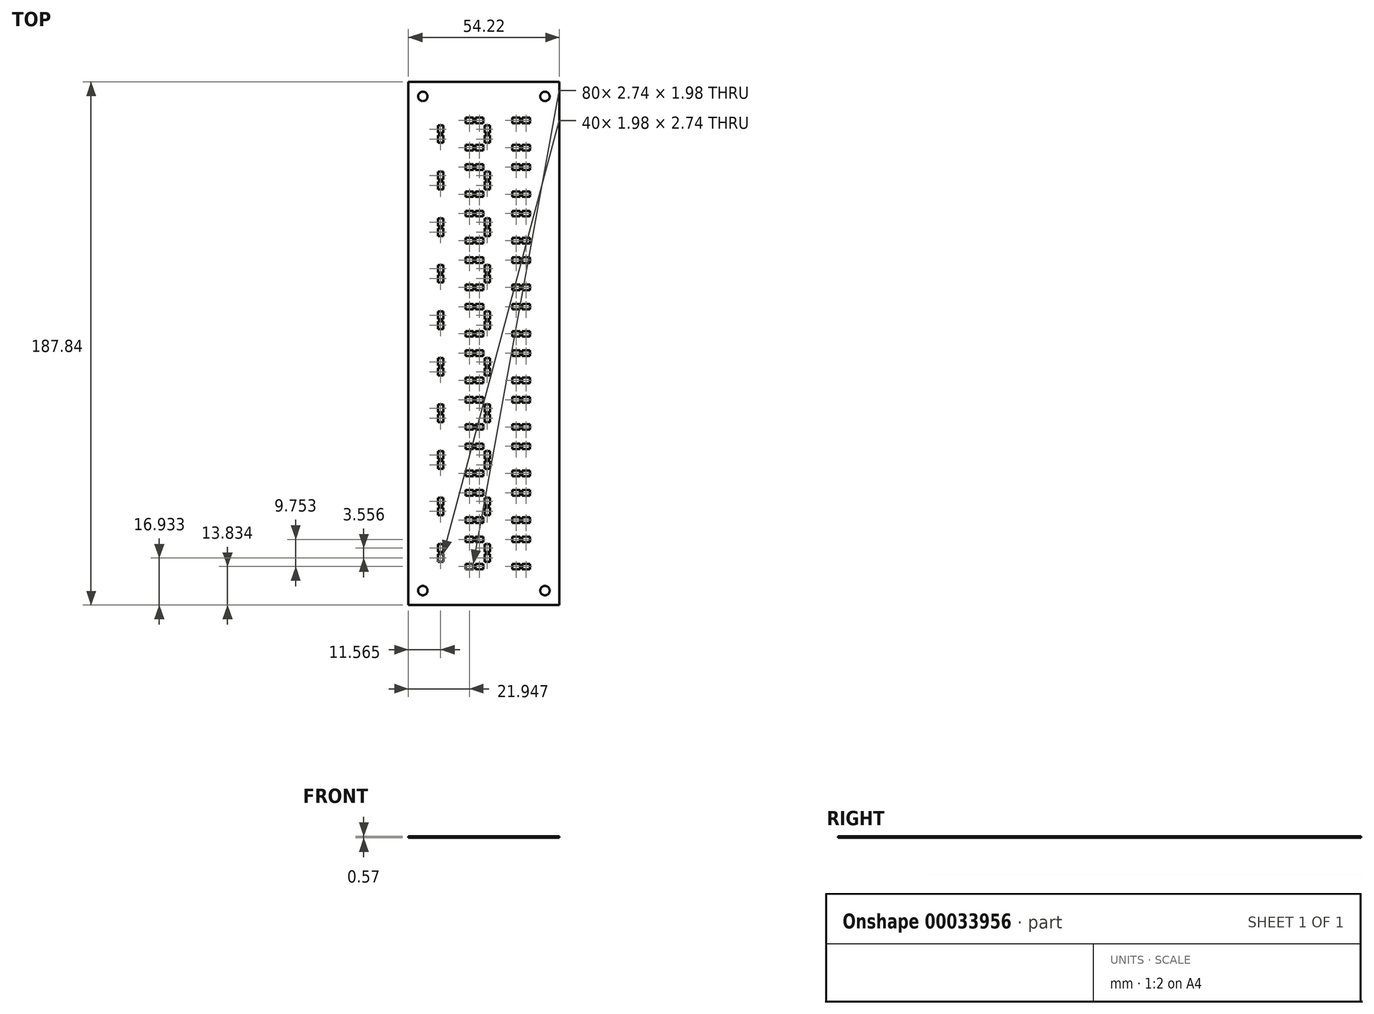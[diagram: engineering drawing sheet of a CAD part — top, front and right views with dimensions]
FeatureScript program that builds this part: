
annotation { "Feature Type Name" : "Feature", "Feature Type Description" : "" }
export const myFeature = defineFeature(function(context is Context, id is Id, definition is map)
    precondition{}
    {
        {
            var Q0;
            Q0=qCreatedBy(makeId("Top.planeOp"),FACE);
            var sketch = newSketch(context, id + "F0", { "sketchPlane" : qUnion([Q0])});
            skLineSegment(sketch, "E0.rect.bottom", {"start": v(-27.11, 93.92) * mm, "end": v(27.11, 93.92) * mm});
            skLineSegment(sketch, "E0.rect.top", {"start": v(-27.11, -93.92) * mm, "end": v(27.11, -93.92) * mm});
            skLineSegment(sketch, "E0.rect.left", {"start": v(-27.11, 93.92) * mm, "end": v(-27.11, -93.92) * mm});
            skLineSegment(sketch, "E0.rect.right", {"start": v(27.11, 93.92) * mm, "end": v(27.11, -93.92) * mm});
            skPoint(sketch, "E0.rect.middle", {"position": v(0, 0) * mm});
            skCircle(sketch, "E1", {"center": v(-21.92, 88.72) * mm, "radius": 1.69 * mm});
            skCircle(sketch, "E2", {"center": v(21.92, 88.72) * mm, "radius": 1.69 * mm});
            skCircle(sketch, "E3", {"center": v(21.92, -88.72) * mm, "radius": 1.69 * mm});
            skCircle(sketch, "E4", {"center": v(-21.92, -88.72) * mm, "radius": 1.69 * mm});
            skSolve(sketch);
        }
        {
            var Q0;
            Q0=qSketchRegion(id+"F0",true);
            extrude(context, id + "F1", {"entities" : qUnion([Q0]), "depth" : .57 * mm});
        }
        {
            var Q0;
            Q0=makeQuery(id+"F1.opExtrude","CAP_FACE",FACE,{"disambiguationData":[OSD([sQuery(id+"F0.wireOp",EDGE,"E0.rect.bottom"),sQuery(id+"F0.wireOp",EDGE,"E0.rect.top"),sQuery(id+"F0.wireOp",EDGE,"E0.rect.left"),sQuery(id+"F0.wireOp",EDGE,"E0.rect.right"),sQuery(id+"F0.wireOp",EDGE,"E1"),sQuery(id+"F0.wireOp",EDGE,"E2"),sQuery(id+"F0.wireOp",EDGE,"E3"),sQuery(id+"F0.wireOp",EDGE,"E4")])],"isStart":false});
            var sketch = newSketch(context, id + "F2", { "sketchPlane" : qUnion([Q0])});
            skLineSegment(sketch, "E5.bottom", {"start": v(-16.54, -78.36) * mm, "end": v(-14.55, -78.36) * mm});
            skLineSegment(sketch, "E5.top", {"start": v(-16.54, -75.62) * mm, "end": v(-14.55, -75.62) * mm});
            skLineSegment(sketch, "E5.left", {"start": v(-16.54, -78.36) * mm, "end": v(-16.54, -75.62) * mm});
            skLineSegment(sketch, "E5.right", {"start": v(-14.55, -78.36) * mm, "end": v(-14.55, -75.62) * mm});
            skLineSegment(sketch, "E6.bottom", {"start": v(-6.53, -79.1) * mm, "end": v(-3.8, -79.1) * mm});
            skLineSegment(sketch, "E6.top", {"start": v(-6.53, -81.08) * mm, "end": v(-3.8, -81.08) * mm});
            skLineSegment(sketch, "E6.left", {"start": v(-6.53, -79.1) * mm, "end": v(-6.53, -81.08) * mm});
            skLineSegment(sketch, "E6.right", {"start": v(-3.8, -79.1) * mm, "end": v(-3.8, -81.08) * mm});
            skLineSegment(sketch, "E7.bottom", {"start": v(-16.54, -74.8) * mm, "end": v(-14.55, -74.8) * mm});
            skLineSegment(sketch, "E7.top", {"start": v(-16.54, -72.06) * mm, "end": v(-14.55, -72.06) * mm});
            skLineSegment(sketch, "E7.left", {"start": v(-16.54, -74.8) * mm, "end": v(-16.54, -72.06) * mm});
            skLineSegment(sketch, "E7.right", {"start": v(-14.55, -74.8) * mm, "end": v(-14.55, -72.06) * mm});
            skLineSegment(sketch, "E8.left", {"start": v(-2.98, -79.1) * mm, "end": v(-2.98, -81.08) * mm});
            skLineSegment(sketch, "E8.top", {"start": v(-2.98, -81.08) * mm, "end": v(-0.24, -81.08) * mm});
            skLineSegment(sketch, "E8.right", {"start": v(-0.24, -79.1) * mm, "end": v(-0.24, -81.08) * mm});
            skLineSegment(sketch, "E8.bottom", {"start": v(-2.98, -79.1) * mm, "end": v(-0.24, -79.1) * mm});
            skLineSegment(sketch, "E9.top", {"start": v(-2.98, -71.32) * mm, "end": v(-0.24, -71.32) * mm});
            skLineSegment(sketch, "E10.right", {"start": v(-3.8, -69.34) * mm, "end": v(-3.8, -71.32) * mm});
            skLineSegment(sketch, "E9.left", {"start": v(-2.98, -69.34) * mm, "end": v(-2.98, -71.32) * mm});
            skLineSegment(sketch, "E10.top", {"start": v(-6.53, -71.32) * mm, "end": v(-3.8, -71.32) * mm});
            skLineSegment(sketch, "E10.bottom", {"start": v(-6.53, -69.34) * mm, "end": v(-3.8, -69.34) * mm});
            skLineSegment(sketch, "E9.bottom", {"start": v(-2.98, -69.34) * mm, "end": v(-0.24, -69.34) * mm});
            skLineSegment(sketch, "E9.right", {"start": v(-0.24, -69.34) * mm, "end": v(-0.24, -71.32) * mm});
            skLineSegment(sketch, "E10.left", {"start": v(-6.53, -69.34) * mm, "end": v(-6.53, -71.32) * mm});
            skLineSegment(sketch, "E11.top", {"start": v(13.79, -71.32) * mm, "end": v(16.53, -71.32) * mm});
            skLineSegment(sketch, "E12.top", {"start": v(13.79, -81.08) * mm, "end": v(16.53, -81.08) * mm});
            skLineSegment(sketch, "E11.right", {"start": v(16.53, -69.34) * mm, "end": v(16.53, -71.32) * mm});
            skLineSegment(sketch, "E11.bottom", {"start": v(13.79, -69.34) * mm, "end": v(16.53, -69.34) * mm});
            skLineSegment(sketch, "E13.right", {"start": v(2.21, -78.36) * mm, "end": v(2.21, -75.62) * mm});
            skLineSegment(sketch, "E13.left", {"start": v(0.23, -78.36) * mm, "end": v(0.23, -75.62) * mm});
            skLineSegment(sketch, "E13.top", {"start": v(0.23, -75.62) * mm, "end": v(2.21, -75.62) * mm});
            skLineSegment(sketch, "E13.bottom", {"start": v(0.23, -78.36) * mm, "end": v(2.21, -78.36) * mm});
            skLineSegment(sketch, "E12.bottom", {"start": v(13.79, -79.1) * mm, "end": v(16.53, -79.1) * mm});
            skLineSegment(sketch, "E12.right", {"start": v(16.53, -79.1) * mm, "end": v(16.53, -81.08) * mm});
            skLineSegment(sketch, "E14.top", {"start": v(0.23, -72.06) * mm, "end": v(2.21, -72.06) * mm});
            skLineSegment(sketch, "E14.bottom", {"start": v(0.23, -74.8) * mm, "end": v(2.21, -74.8) * mm});
            skLineSegment(sketch, "E11.left", {"start": v(13.79, -69.34) * mm, "end": v(13.79, -71.32) * mm});
            skLineSegment(sketch, "E15.bottom", {"start": v(10.23, -69.34) * mm, "end": v(12.98, -69.34) * mm});
            skLineSegment(sketch, "E15.right", {"start": v(12.98, -69.34) * mm, "end": v(12.98, -71.32) * mm});
            skLineSegment(sketch, "E15.top", {"start": v(10.23, -71.32) * mm, "end": v(12.98, -71.32) * mm});
            skLineSegment(sketch, "E15.left", {"start": v(10.23, -69.34) * mm, "end": v(10.23, -71.32) * mm});
            skLineSegment(sketch, "E12.left", {"start": v(13.79, -79.1) * mm, "end": v(13.79, -81.08) * mm});
            skLineSegment(sketch, "E14.right", {"start": v(2.21, -74.8) * mm, "end": v(2.21, -72.06) * mm});
            skLineSegment(sketch, "E16.left", {"start": v(10.23, -79.1) * mm, "end": v(10.23, -81.08) * mm});
            skLineSegment(sketch, "E16.top", {"start": v(10.23, -81.08) * mm, "end": v(12.98, -81.08) * mm});
            skLineSegment(sketch, "E16.bottom", {"start": v(10.23, -79.1) * mm, "end": v(12.98, -79.1) * mm});
            skLineSegment(sketch, "E14.left", {"start": v(0.23, -74.8) * mm, "end": v(0.23, -72.06) * mm});
            skLineSegment(sketch, "E16.right", {"start": v(12.98, -79.1) * mm, "end": v(12.98, -81.08) * mm});
            skLineSegment(sketch, "E17.left", {"start": v(0.23, -61.65) * mm, "end": v(0.23, -58.9) * mm});
            skLineSegment(sketch, "E18.bottom", {"start": v(-16.54, -61.65) * mm, "end": v(-14.55, -61.65) * mm});
            skLineSegment(sketch, "E19.right", {"start": v(-0.24, -62.38) * mm, "end": v(-0.24, -64.36) * mm});
            skLineSegment(sketch, "E18.top", {"start": v(-16.54, -58.9) * mm, "end": v(-14.55, -58.9) * mm});
            skLineSegment(sketch, "E20.top", {"start": v(-2.98, -54.61) * mm, "end": v(-0.24, -54.61) * mm});
            skLineSegment(sketch, "E19.top", {"start": v(-2.98, -64.36) * mm, "end": v(-0.24, -64.36) * mm});
            skLineSegment(sketch, "E17.right", {"start": v(2.21, -61.65) * mm, "end": v(2.21, -58.9) * mm});
            skLineSegment(sketch, "E21.top", {"start": v(13.79, -54.61) * mm, "end": v(16.53, -54.61) * mm});
            skLineSegment(sketch, "E17.top", {"start": v(0.23, -58.9) * mm, "end": v(2.21, -58.9) * mm});
            skLineSegment(sketch, "E22.right", {"start": v(16.53, -62.38) * mm, "end": v(16.53, -64.36) * mm});
            skLineSegment(sketch, "E18.left", {"start": v(-16.54, -61.65) * mm, "end": v(-16.54, -58.9) * mm});
            skLineSegment(sketch, "E18.right", {"start": v(-14.55, -61.65) * mm, "end": v(-14.55, -58.9) * mm});
            skLineSegment(sketch, "E23.bottom", {"start": v(-16.54, -58.09) * mm, "end": v(-14.55, -58.09) * mm});
            skLineSegment(sketch, "E23.top", {"start": v(-16.54, -55.35) * mm, "end": v(-14.55, -55.35) * mm});
            skLineSegment(sketch, "E22.top", {"start": v(13.79, -64.36) * mm, "end": v(16.53, -64.36) * mm});
            skLineSegment(sketch, "E17.bottom", {"start": v(0.23, -61.65) * mm, "end": v(2.21, -61.65) * mm});
            skLineSegment(sketch, "E24.top", {"start": v(0.23, -55.35) * mm, "end": v(2.21, -55.35) * mm});
            skLineSegment(sketch, "E21.right", {"start": v(16.53, -52.63) * mm, "end": v(16.53, -54.61) * mm});
            skLineSegment(sketch, "E24.bottom", {"start": v(0.23, -58.09) * mm, "end": v(2.21, -58.09) * mm});
            skLineSegment(sketch, "E25.top", {"start": v(10.23, -54.61) * mm, "end": v(12.98, -54.61) * mm});
            skLineSegment(sketch, "E21.bottom", {"start": v(13.79, -52.63) * mm, "end": v(16.53, -52.63) * mm});
            skLineSegment(sketch, "E26.left", {"start": v(10.23, -62.38) * mm, "end": v(10.23, -64.36) * mm});
            skLineSegment(sketch, "E21.left", {"start": v(13.79, -52.63) * mm, "end": v(13.79, -54.61) * mm});
            skLineSegment(sketch, "E27.right", {"start": v(-3.8, -52.63) * mm, "end": v(-3.8, -54.61) * mm});
            skLineSegment(sketch, "E19.bottom", {"start": v(-2.98, -62.38) * mm, "end": v(-0.24, -62.38) * mm});
            skLineSegment(sketch, "E27.left", {"start": v(-6.53, -52.63) * mm, "end": v(-6.53, -54.61) * mm});
            skLineSegment(sketch, "E27.bottom", {"start": v(-6.53, -52.63) * mm, "end": v(-3.8, -52.63) * mm});
            skLineSegment(sketch, "E26.bottom", {"start": v(10.23, -62.38) * mm, "end": v(12.98, -62.38) * mm});
            skLineSegment(sketch, "E22.bottom", {"start": v(13.79, -62.38) * mm, "end": v(16.53, -62.38) * mm});
            skLineSegment(sketch, "E26.top", {"start": v(10.23, -64.36) * mm, "end": v(12.98, -64.36) * mm});
            skLineSegment(sketch, "E25.left", {"start": v(10.23, -52.63) * mm, "end": v(10.23, -54.61) * mm});
            skLineSegment(sketch, "E25.bottom", {"start": v(10.23, -52.63) * mm, "end": v(12.98, -52.63) * mm});
            skLineSegment(sketch, "E20.bottom", {"start": v(-2.98, -52.63) * mm, "end": v(-0.24, -52.63) * mm});
            skLineSegment(sketch, "E24.left", {"start": v(0.23, -58.09) * mm, "end": v(0.23, -55.35) * mm});
            skLineSegment(sketch, "E28.bottom", {"start": v(-6.53, -62.38) * mm, "end": v(-3.8, -62.38) * mm});
            skLineSegment(sketch, "E28.top", {"start": v(-6.53, -64.36) * mm, "end": v(-3.8, -64.36) * mm});
            skLineSegment(sketch, "E28.left", {"start": v(-6.53, -62.38) * mm, "end": v(-6.53, -64.36) * mm});
            skLineSegment(sketch, "E28.right", {"start": v(-3.8, -62.38) * mm, "end": v(-3.8, -64.36) * mm});
            skLineSegment(sketch, "E23.left", {"start": v(-16.54, -58.09) * mm, "end": v(-16.54, -55.35) * mm});
            skLineSegment(sketch, "E23.right", {"start": v(-14.55, -58.09) * mm, "end": v(-14.55, -55.35) * mm});
            skLineSegment(sketch, "E22.left", {"start": v(13.79, -62.38) * mm, "end": v(13.79, -64.36) * mm});
            skLineSegment(sketch, "E19.left", {"start": v(-2.98, -62.38) * mm, "end": v(-2.98, -64.36) * mm});
            skLineSegment(sketch, "E25.right", {"start": v(12.98, -52.63) * mm, "end": v(12.98, -54.61) * mm});
            skLineSegment(sketch, "E20.right", {"start": v(-0.24, -52.63) * mm, "end": v(-0.24, -54.61) * mm});
            skLineSegment(sketch, "E26.right", {"start": v(12.98, -62.38) * mm, "end": v(12.98, -64.36) * mm});
            skLineSegment(sketch, "E20.left", {"start": v(-2.98, -52.63) * mm, "end": v(-2.98, -54.61) * mm});
            skLineSegment(sketch, "E24.right", {"start": v(2.21, -58.09) * mm, "end": v(2.21, -55.35) * mm});
            skLineSegment(sketch, "E27.top", {"start": v(-6.53, -54.61) * mm, "end": v(-3.8, -54.61) * mm});
            skLineSegment(sketch, "E29.top", {"start": v(0.23, -25.48) * mm, "end": v(2.21, -25.48) * mm});
            skLineSegment(sketch, "E30.top", {"start": v(13.79, -37.9) * mm, "end": v(16.53, -37.9) * mm});
            skLineSegment(sketch, "E31.top", {"start": v(0.23, -38.63) * mm, "end": v(2.21, -38.63) * mm});
            skLineSegment(sketch, "E32.top", {"start": v(13.79, -47.65) * mm, "end": v(16.53, -47.65) * mm});
            skLineSegment(sketch, "E33.top", {"start": v(-2.98, -47.65) * mm, "end": v(-0.24, -47.65) * mm});
            skLineSegment(sketch, "E34.bottom", {"start": v(0.23, -24.66) * mm, "end": v(2.21, -24.66) * mm});
            skLineSegment(sketch, "E35.left", {"start": v(-16.54, -28.22) * mm, "end": v(-16.54, -25.48) * mm});
            skLineSegment(sketch, "E30.right", {"start": v(16.53, -35.92) * mm, "end": v(16.53, -37.9) * mm});
            skLineSegment(sketch, "E31.bottom", {"start": v(0.23, -41.38) * mm, "end": v(2.21, -41.38) * mm});
            skLineSegment(sketch, "E36.left", {"start": v(-16.54, -44.93) * mm, "end": v(-16.54, -42.19) * mm});
            skLineSegment(sketch, "E36.right", {"start": v(-14.55, -44.93) * mm, "end": v(-14.55, -42.19) * mm});
            skLineSegment(sketch, "E37.top", {"start": v(-2.98, -37.9) * mm, "end": v(-0.24, -37.9) * mm});
            skLineSegment(sketch, "E38.top", {"start": v(13.79, -21.18) * mm, "end": v(16.53, -21.18) * mm});
            skLineSegment(sketch, "E29.left", {"start": v(0.23, -28.22) * mm, "end": v(0.23, -25.48) * mm});
            skLineSegment(sketch, "E34.top", {"start": v(0.23, -21.92) * mm, "end": v(2.21, -21.92) * mm});
            skLineSegment(sketch, "E29.right", {"start": v(2.21, -28.22) * mm, "end": v(2.21, -25.48) * mm});
            skLineSegment(sketch, "E29.bottom", {"start": v(0.23, -28.22) * mm, "end": v(2.21, -28.22) * mm});
            skLineSegment(sketch, "E39.bottom", {"start": v(0.23, -44.93) * mm, "end": v(2.21, -44.93) * mm});
            skLineSegment(sketch, "E40.top", {"start": v(-2.98, -30.94) * mm, "end": v(-0.24, -30.94) * mm});
            skLineSegment(sketch, "E41.top", {"start": v(13.79, -30.94) * mm, "end": v(16.53, -30.94) * mm});
            skLineSegment(sketch, "E39.top", {"start": v(0.23, -42.19) * mm, "end": v(2.21, -42.19) * mm});
            skLineSegment(sketch, "E39.right", {"start": v(2.21, -44.93) * mm, "end": v(2.21, -42.19) * mm});
            skLineSegment(sketch, "E42.top", {"start": v(-2.98, -21.18) * mm, "end": v(-0.24, -21.18) * mm});
            skLineSegment(sketch, "E39.left", {"start": v(0.23, -44.93) * mm, "end": v(0.23, -42.19) * mm});
            skLineSegment(sketch, "E35.right", {"start": v(-14.55, -28.22) * mm, "end": v(-14.55, -25.48) * mm});
            skLineSegment(sketch, "E43.left", {"start": v(10.23, -35.92) * mm, "end": v(10.23, -37.9) * mm});
            skLineSegment(sketch, "E44.top", {"start": v(-6.53, -47.65) * mm, "end": v(-3.8, -47.65) * mm});
            skLineSegment(sketch, "E33.bottom", {"start": v(-2.98, -45.67) * mm, "end": v(-0.24, -45.67) * mm});
            skLineSegment(sketch, "E37.left", {"start": v(-2.98, -35.92) * mm, "end": v(-2.98, -37.9) * mm});
            skLineSegment(sketch, "E45.right", {"start": v(-14.55, -41.38) * mm, "end": v(-14.55, -38.63) * mm});
            skLineSegment(sketch, "E46.right", {"start": v(-3.8, -35.92) * mm, "end": v(-3.8, -37.9) * mm});
            skLineSegment(sketch, "E34.left", {"start": v(0.23, -24.66) * mm, "end": v(0.23, -21.92) * mm});
            skLineSegment(sketch, "E45.left", {"start": v(-16.54, -41.38) * mm, "end": v(-16.54, -38.63) * mm});
            skLineSegment(sketch, "E47.bottom", {"start": v(-6.53, -28.96) * mm, "end": v(-3.8, -28.96) * mm});
            skLineSegment(sketch, "E48.bottom", {"start": v(-6.53, -19.2) * mm, "end": v(-3.8, -19.2) * mm});
            skLineSegment(sketch, "E31.right", {"start": v(2.21, -41.38) * mm, "end": v(2.21, -38.63) * mm});
            skLineSegment(sketch, "E46.top", {"start": v(-6.53, -37.9) * mm, "end": v(-3.8, -37.9) * mm});
            skLineSegment(sketch, "E49.top", {"start": v(10.23, -21.18) * mm, "end": v(12.98, -21.18) * mm});
            skLineSegment(sketch, "E47.top", {"start": v(-6.53, -30.94) * mm, "end": v(-3.8, -30.94) * mm});
            skLineSegment(sketch, "E44.bottom", {"start": v(-6.53, -45.67) * mm, "end": v(-3.8, -45.67) * mm});
            skLineSegment(sketch, "E40.bottom", {"start": v(-2.98, -28.96) * mm, "end": v(-0.24, -28.96) * mm});
            skLineSegment(sketch, "E50.right", {"start": v(-14.55, -24.66) * mm, "end": v(-14.55, -21.92) * mm});
            skLineSegment(sketch, "E32.bottom", {"start": v(13.79, -45.67) * mm, "end": v(16.53, -45.67) * mm});
            skLineSegment(sketch, "E46.left", {"start": v(-6.53, -35.92) * mm, "end": v(-6.53, -37.9) * mm});
            skLineSegment(sketch, "E43.top", {"start": v(10.23, -37.9) * mm, "end": v(12.98, -37.9) * mm});
            skLineSegment(sketch, "E42.bottom", {"start": v(-2.98, -19.2) * mm, "end": v(-0.24, -19.2) * mm});
            skLineSegment(sketch, "E49.bottom", {"start": v(10.23, -19.2) * mm, "end": v(12.98, -19.2) * mm});
            skLineSegment(sketch, "E50.left", {"start": v(-16.54, -24.66) * mm, "end": v(-16.54, -21.92) * mm});
            skLineSegment(sketch, "E48.top", {"start": v(-6.53, -21.18) * mm, "end": v(-3.8, -21.18) * mm});
            skLineSegment(sketch, "E37.right", {"start": v(-0.24, -35.92) * mm, "end": v(-0.24, -37.9) * mm});
            skLineSegment(sketch, "E43.right", {"start": v(12.98, -35.92) * mm, "end": v(12.98, -37.9) * mm});
            skLineSegment(sketch, "E31.left", {"start": v(0.23, -41.38) * mm, "end": v(0.23, -38.63) * mm});
            skLineSegment(sketch, "E34.right", {"start": v(2.21, -24.66) * mm, "end": v(2.21, -21.92) * mm});
            skLineSegment(sketch, "E37.bottom", {"start": v(-2.98, -35.92) * mm, "end": v(-0.24, -35.92) * mm});
            skLineSegment(sketch, "E43.bottom", {"start": v(10.23, -35.92) * mm, "end": v(12.98, -35.92) * mm});
            skLineSegment(sketch, "E51.top", {"start": v(10.23, -47.65) * mm, "end": v(12.98, -47.65) * mm});
            skLineSegment(sketch, "E41.bottom", {"start": v(13.79, -28.96) * mm, "end": v(16.53, -28.96) * mm});
            skLineSegment(sketch, "E51.bottom", {"start": v(10.23, -45.67) * mm, "end": v(12.98, -45.67) * mm});
            skLineSegment(sketch, "E38.bottom", {"start": v(13.79, -19.2) * mm, "end": v(16.53, -19.2) * mm});
            skLineSegment(sketch, "E52.top", {"start": v(10.23, -30.94) * mm, "end": v(12.98, -30.94) * mm});
            skLineSegment(sketch, "E46.bottom", {"start": v(-6.53, -35.92) * mm, "end": v(-3.8, -35.92) * mm});
            skLineSegment(sketch, "E30.left", {"start": v(13.79, -35.92) * mm, "end": v(13.79, -37.9) * mm});
            skLineSegment(sketch, "E30.bottom", {"start": v(13.79, -35.92) * mm, "end": v(16.53, -35.92) * mm});
            skLineSegment(sketch, "E52.bottom", {"start": v(10.23, -28.96) * mm, "end": v(12.98, -28.96) * mm});
            skLineSegment(sketch, "E33.left", {"start": v(-2.98, -45.67) * mm, "end": v(-2.98, -47.65) * mm});
            skLineSegment(sketch, "E41.left", {"start": v(13.79, -28.96) * mm, "end": v(13.79, -30.94) * mm});
            skLineSegment(sketch, "E32.left", {"start": v(13.79, -45.67) * mm, "end": v(13.79, -47.65) * mm});
            skLineSegment(sketch, "E44.left", {"start": v(-6.53, -45.67) * mm, "end": v(-6.53, -47.65) * mm});
            skLineSegment(sketch, "E36.top", {"start": v(-16.54, -42.19) * mm, "end": v(-14.55, -42.19) * mm});
            skLineSegment(sketch, "E45.bottom", {"start": v(-16.54, -41.38) * mm, "end": v(-14.55, -41.38) * mm});
            skLineSegment(sketch, "E32.right", {"start": v(16.53, -45.67) * mm, "end": v(16.53, -47.65) * mm});
            skLineSegment(sketch, "E36.bottom", {"start": v(-16.54, -44.93) * mm, "end": v(-14.55, -44.93) * mm});
            skLineSegment(sketch, "E40.left", {"start": v(-2.98, -28.96) * mm, "end": v(-2.98, -30.94) * mm});
            skLineSegment(sketch, "E35.bottom", {"start": v(-16.54, -28.22) * mm, "end": v(-14.55, -28.22) * mm});
            skLineSegment(sketch, "E44.right", {"start": v(-3.8, -45.67) * mm, "end": v(-3.8, -47.65) * mm});
            skLineSegment(sketch, "E48.left", {"start": v(-6.53, -19.2) * mm, "end": v(-6.53, -21.18) * mm});
            skLineSegment(sketch, "E33.right", {"start": v(-0.24, -45.67) * mm, "end": v(-0.24, -47.65) * mm});
            skLineSegment(sketch, "E41.right", {"start": v(16.53, -28.96) * mm, "end": v(16.53, -30.94) * mm});
            skLineSegment(sketch, "E38.right", {"start": v(16.53, -19.2) * mm, "end": v(16.53, -21.18) * mm});
            skLineSegment(sketch, "E45.top", {"start": v(-16.54, -38.63) * mm, "end": v(-14.55, -38.63) * mm});
            skLineSegment(sketch, "E40.right", {"start": v(-0.24, -28.96) * mm, "end": v(-0.24, -30.94) * mm});
            skLineSegment(sketch, "E49.right", {"start": v(12.98, -19.2) * mm, "end": v(12.98, -21.18) * mm});
            skLineSegment(sketch, "E35.top", {"start": v(-16.54, -25.48) * mm, "end": v(-14.55, -25.48) * mm});
            skLineSegment(sketch, "E48.right", {"start": v(-3.8, -19.2) * mm, "end": v(-3.8, -21.18) * mm});
            skLineSegment(sketch, "E51.right", {"start": v(12.98, -45.67) * mm, "end": v(12.98, -47.65) * mm});
            skLineSegment(sketch, "E38.left", {"start": v(13.79, -19.2) * mm, "end": v(13.79, -21.18) * mm});
            skLineSegment(sketch, "E52.left", {"start": v(10.23, -28.96) * mm, "end": v(10.23, -30.94) * mm});
            skLineSegment(sketch, "E47.right", {"start": v(-3.8, -28.96) * mm, "end": v(-3.8, -30.94) * mm});
            skLineSegment(sketch, "E49.left", {"start": v(10.23, -19.2) * mm, "end": v(10.23, -21.18) * mm});
            skLineSegment(sketch, "E52.right", {"start": v(12.98, -28.96) * mm, "end": v(12.98, -30.94) * mm});
            skLineSegment(sketch, "E50.bottom", {"start": v(-16.54, -24.66) * mm, "end": v(-14.55, -24.66) * mm});
            skLineSegment(sketch, "E50.top", {"start": v(-16.54, -21.92) * mm, "end": v(-14.55, -21.92) * mm});
            skLineSegment(sketch, "E47.left", {"start": v(-6.53, -28.96) * mm, "end": v(-6.53, -30.94) * mm});
            skLineSegment(sketch, "E42.left", {"start": v(-2.98, -19.2) * mm, "end": v(-2.98, -21.18) * mm});
            skLineSegment(sketch, "E42.right", {"start": v(-0.24, -19.2) * mm, "end": v(-0.24, -21.18) * mm});
            skLineSegment(sketch, "E51.left", {"start": v(10.23, -45.67) * mm, "end": v(10.23, -47.65) * mm});
            skLineSegment(sketch, "E53.left", {"start": v(0.23, 38.63) * mm, "end": v(0.23, 41.38) * mm});
            skLineSegment(sketch, "E54.bottom", {"start": v(0.23, 21.92) * mm, "end": v(2.21, 21.92) * mm});
            skLineSegment(sketch, "E55.right", {"start": v(-14.55, 25.48) * mm, "end": v(-14.55, 28.22) * mm});
            skLineSegment(sketch, "E56.right", {"start": v(-0.24, 21.18) * mm, "end": v(-0.24, 19.2) * mm});
            skLineSegment(sketch, "E57.left", {"start": v(0.23, -11.5) * mm, "end": v(0.23, -8.76) * mm});
            skLineSegment(sketch, "E58.left", {"start": v(10.23, -12.24) * mm, "end": v(10.23, -14.22) * mm});
            skLineSegment(sketch, "E59.right", {"start": v(-14.55, 5.2) * mm, "end": v(-14.55, 7.95) * mm});
            skLineSegment(sketch, "E60.right", {"start": v(-0.24, 37.9) * mm, "end": v(-0.24, 35.91) * mm});
            skLineSegment(sketch, "E53.bottom", {"start": v(0.23, 38.63) * mm, "end": v(2.21, 38.63) * mm});
            skLineSegment(sketch, "E55.left", {"start": v(-16.54, 25.48) * mm, "end": v(-16.54, 28.22) * mm});
            skLineSegment(sketch, "E57.right", {"start": v(2.21, -11.5) * mm, "end": v(2.21, -8.76) * mm});
            skLineSegment(sketch, "E58.top", {"start": v(10.23, -14.22) * mm, "end": v(12.98, -14.22) * mm});
            skLineSegment(sketch, "E61.right", {"start": v(16.53, -12.24) * mm, "end": v(16.53, -14.22) * mm});
            skLineSegment(sketch, "E62.right", {"start": v(-0.24, 4.47) * mm, "end": v(-0.24, 2.49) * mm});
            skLineSegment(sketch, "E60.top", {"start": v(-2.98, 35.91) * mm, "end": v(-0.24, 35.91) * mm});
            skLineSegment(sketch, "E57.bottom", {"start": v(0.23, -11.5) * mm, "end": v(2.21, -11.5) * mm});
            skLineSegment(sketch, "E63.bottom", {"start": v(0.23, 5.2) * mm, "end": v(2.21, 5.2) * mm});
            skLineSegment(sketch, "E58.right", {"start": v(12.98, -12.24) * mm, "end": v(12.98, -14.22) * mm});
            skLineSegment(sketch, "E53.right", {"start": v(2.21, 38.63) * mm, "end": v(2.21, 41.38) * mm});
            skLineSegment(sketch, "E53.top", {"start": v(0.23, 41.38) * mm, "end": v(2.21, 41.38) * mm});
            skLineSegment(sketch, "E56.top", {"start": v(-2.98, 19.2) * mm, "end": v(-0.24, 19.2) * mm});
            skLineSegment(sketch, "E64.right", {"start": v(2.21, 42.19) * mm, "end": v(2.21, 44.93) * mm});
            skLineSegment(sketch, "E64.bottom", {"start": v(0.23, 42.19) * mm, "end": v(2.21, 42.19) * mm});
            skLineSegment(sketch, "E62.top", {"start": v(-2.98, 2.49) * mm, "end": v(-0.24, 2.49) * mm});
            skLineSegment(sketch, "E54.right", {"start": v(2.21, 21.92) * mm, "end": v(2.21, 24.66) * mm});
            skLineSegment(sketch, "E65.left", {"start": v(-16.54, 38.63) * mm, "end": v(-16.54, 41.38) * mm});
            skLineSegment(sketch, "E66.left", {"start": v(-16.54, 8.76) * mm, "end": v(-16.54, 11.5) * mm});
            skLineSegment(sketch, "E63.right", {"start": v(2.21, 5.2) * mm, "end": v(2.21, 7.95) * mm});
            skLineSegment(sketch, "E66.right", {"start": v(-14.55, 8.76) * mm, "end": v(-14.55, 11.5) * mm});
            skLineSegment(sketch, "E65.right", {"start": v(-14.55, 38.63) * mm, "end": v(-14.55, 41.38) * mm});
            skLineSegment(sketch, "E67.top", {"start": v(-2.98, -14.22) * mm, "end": v(-0.24, -14.22) * mm});
            skLineSegment(sketch, "E67.right", {"start": v(-0.24, -12.24) * mm, "end": v(-0.24, -14.22) * mm});
            skLineSegment(sketch, "E68.left", {"start": v(-16.54, -11.5) * mm, "end": v(-16.54, -8.76) * mm});
            skLineSegment(sketch, "E68.right", {"start": v(-14.55, -11.5) * mm, "end": v(-14.55, -8.76) * mm});
            skLineSegment(sketch, "E69.top", {"start": v(-6.53, -14.22) * mm, "end": v(-3.8, -14.22) * mm});
            skLineSegment(sketch, "E69.left", {"start": v(-6.53, -12.24) * mm, "end": v(-6.53, -14.22) * mm});
            skLineSegment(sketch, "E69.right", {"start": v(-3.8, -12.24) * mm, "end": v(-3.8, -14.22) * mm});
            skLineSegment(sketch, "E61.left", {"start": v(13.79, -12.24) * mm, "end": v(13.79, -14.22) * mm});
            skLineSegment(sketch, "E61.top", {"start": v(13.79, -14.22) * mm, "end": v(16.53, -14.22) * mm});
            skLineSegment(sketch, "E67.left", {"start": v(-2.98, -12.24) * mm, "end": v(-2.98, -14.22) * mm});
            skLineSegment(sketch, "E70.right", {"start": v(-14.55, 21.92) * mm, "end": v(-14.55, 24.66) * mm});
            skLineSegment(sketch, "E71.bottom", {"start": v(13.79, 4.47) * mm, "end": v(16.53, 4.47) * mm});
            skLineSegment(sketch, "E72.bottom", {"start": v(10.23, 47.65) * mm, "end": v(12.98, 47.65) * mm});
            skLineSegment(sketch, "E73.bottom", {"start": v(13.79, 30.94) * mm, "end": v(16.53, 30.94) * mm});
            skLineSegment(sketch, "E72.right", {"start": v(12.98, 47.65) * mm, "end": v(12.98, 45.67) * mm});
            skLineSegment(sketch, "E74.right", {"start": v(-0.24, 30.94) * mm, "end": v(-0.24, 28.95) * mm});
            skLineSegment(sketch, "E75.bottom", {"start": v(-6.53, 30.94) * mm, "end": v(-3.8, 30.94) * mm});
            skLineSegment(sketch, "E76.left", {"start": v(0.23, -7.95) * mm, "end": v(0.23, -5.2) * mm});
            skLineSegment(sketch, "E77.left", {"start": v(13.79, 37.9) * mm, "end": v(13.79, 35.91) * mm});
            skLineSegment(sketch, "E77.right", {"start": v(16.53, 37.9) * mm, "end": v(16.53, 35.91) * mm});
            skLineSegment(sketch, "E78.right", {"start": v(2.21, 8.76) * mm, "end": v(2.21, 11.5) * mm});
            skLineSegment(sketch, "E57.top", {"start": v(0.23, -8.76) * mm, "end": v(2.21, -8.76) * mm});
            skLineSegment(sketch, "E66.bottom", {"start": v(-16.54, 8.76) * mm, "end": v(-14.55, 8.76) * mm});
            skLineSegment(sketch, "E71.top", {"start": v(13.79, 2.49) * mm, "end": v(16.53, 2.49) * mm});
            skLineSegment(sketch, "E79.left", {"start": v(10.23, 14.22) * mm, "end": v(10.23, 12.24) * mm});
            skLineSegment(sketch, "E80.bottom", {"start": v(-2.98, 47.65) * mm, "end": v(-0.24, 47.65) * mm});
            skLineSegment(sketch, "E73.left", {"start": v(13.79, 30.94) * mm, "end": v(13.79, 28.95) * mm});
            skLineSegment(sketch, "E58.bottom", {"start": v(10.23, -12.24) * mm, "end": v(12.98, -12.24) * mm});
            skLineSegment(sketch, "E66.top", {"start": v(-16.54, 11.5) * mm, "end": v(-14.55, 11.5) * mm});
            skLineSegment(sketch, "E81.top", {"start": v(10.23, 2.49) * mm, "end": v(12.98, 2.49) * mm});
            skLineSegment(sketch, "E82.top", {"start": v(-2.98, -4.47) * mm, "end": v(-0.24, -4.47) * mm});
            skLineSegment(sketch, "E61.bottom", {"start": v(13.79, -12.24) * mm, "end": v(16.53, -12.24) * mm});
            skLineSegment(sketch, "E81.right", {"start": v(12.98, 4.47) * mm, "end": v(12.98, 2.49) * mm});
            skLineSegment(sketch, "E83.top", {"start": v(13.79, 45.67) * mm, "end": v(16.53, 45.67) * mm});
            skLineSegment(sketch, "E74.left", {"start": v(-2.98, 30.94) * mm, "end": v(-2.98, 28.95) * mm});
            skLineSegment(sketch, "E84.top", {"start": v(10.23, 28.95) * mm, "end": v(12.98, 28.95) * mm});
            skLineSegment(sketch, "E85.top", {"start": v(10.23, 35.91) * mm, "end": v(12.98, 35.91) * mm});
            skLineSegment(sketch, "E86.left", {"start": v(-6.53, 47.65) * mm, "end": v(-6.53, 45.67) * mm});
            skLineSegment(sketch, "E87.top", {"start": v(-16.54, 44.93) * mm, "end": v(-14.55, 44.93) * mm});
            skLineSegment(sketch, "E88.right", {"start": v(-0.24, 14.22) * mm, "end": v(-0.24, 12.24) * mm});
            skLineSegment(sketch, "E74.top", {"start": v(-2.98, 28.95) * mm, "end": v(-0.24, 28.95) * mm});
            skLineSegment(sketch, "E56.bottom", {"start": v(-2.98, 21.18) * mm, "end": v(-0.24, 21.18) * mm});
            skLineSegment(sketch, "E75.left", {"start": v(-6.53, 30.94) * mm, "end": v(-6.53, 28.95) * mm});
            skLineSegment(sketch, "E89.bottom", {"start": v(13.79, -2.5) * mm, "end": v(16.53, -2.5) * mm});
            skLineSegment(sketch, "E81.bottom", {"start": v(10.23, 4.47) * mm, "end": v(12.98, 4.47) * mm});
            skLineSegment(sketch, "E75.right", {"start": v(-3.8, 30.94) * mm, "end": v(-3.8, 28.95) * mm});
            skLineSegment(sketch, "E64.top", {"start": v(0.23, 44.93) * mm, "end": v(2.21, 44.93) * mm});
            skLineSegment(sketch, "E73.top", {"start": v(13.79, 28.95) * mm, "end": v(16.53, 28.95) * mm});
            skLineSegment(sketch, "E78.left", {"start": v(0.23, 8.76) * mm, "end": v(0.23, 11.5) * mm});
            skLineSegment(sketch, "E90.right", {"start": v(16.53, 14.22) * mm, "end": v(16.53, 12.24) * mm});
            skLineSegment(sketch, "E83.right", {"start": v(16.53, 47.65) * mm, "end": v(16.53, 45.67) * mm});
            skLineSegment(sketch, "E59.bottom", {"start": v(-16.54, 5.2) * mm, "end": v(-14.55, 5.2) * mm});
            skLineSegment(sketch, "E65.top", {"start": v(-16.54, 41.38) * mm, "end": v(-14.55, 41.38) * mm});
            skLineSegment(sketch, "E76.top", {"start": v(0.23, -5.2) * mm, "end": v(2.21, -5.2) * mm});
            skLineSegment(sketch, "E82.left", {"start": v(-2.98, -2.5) * mm, "end": v(-2.98, -4.47) * mm});
            skLineSegment(sketch, "E91.top", {"start": v(0.23, 28.22) * mm, "end": v(2.21, 28.22) * mm});
            skLineSegment(sketch, "E92.bottom", {"start": v(-6.53, 4.47) * mm, "end": v(-3.8, 4.47) * mm});
            skLineSegment(sketch, "E78.bottom", {"start": v(0.23, 8.76) * mm, "end": v(2.21, 8.76) * mm});
            skLineSegment(sketch, "E93.left", {"start": v(13.79, 21.18) * mm, "end": v(13.79, 19.2) * mm});
            skLineSegment(sketch, "E84.right", {"start": v(12.98, 30.94) * mm, "end": v(12.98, 28.95) * mm});
            skLineSegment(sketch, "E86.bottom", {"start": v(-6.53, 47.65) * mm, "end": v(-3.8, 47.65) * mm});
            skLineSegment(sketch, "E94.top", {"start": v(-6.53, 12.24) * mm, "end": v(-3.8, 12.24) * mm});
            skLineSegment(sketch, "E79.bottom", {"start": v(10.23, 14.22) * mm, "end": v(12.98, 14.22) * mm});
            skLineSegment(sketch, "E85.bottom", {"start": v(10.23, 37.9) * mm, "end": v(12.98, 37.9) * mm});
            skLineSegment(sketch, "E87.left", {"start": v(-16.54, 42.19) * mm, "end": v(-16.54, 44.93) * mm});
            skLineSegment(sketch, "E64.left", {"start": v(0.23, 42.19) * mm, "end": v(0.23, 44.93) * mm});
            skLineSegment(sketch, "E95.left", {"start": v(10.23, 21.18) * mm, "end": v(10.23, 19.2) * mm});
            skLineSegment(sketch, "E76.bottom", {"start": v(0.23, -7.95) * mm, "end": v(2.21, -7.95) * mm});
            skLineSegment(sketch, "E55.top", {"start": v(-16.54, 28.22) * mm, "end": v(-14.55, 28.22) * mm});
            skLineSegment(sketch, "E96.top", {"start": v(-6.53, -4.47) * mm, "end": v(-3.8, -4.47) * mm});
            skLineSegment(sketch, "E93.top", {"start": v(13.79, 19.2) * mm, "end": v(16.53, 19.2) * mm});
            skLineSegment(sketch, "E79.top", {"start": v(10.23, 12.24) * mm, "end": v(12.98, 12.24) * mm});
            skLineSegment(sketch, "E59.top", {"start": v(-16.54, 7.95) * mm, "end": v(-14.55, 7.95) * mm});
            skLineSegment(sketch, "E91.left", {"start": v(0.23, 25.48) * mm, "end": v(0.23, 28.22) * mm});
            skLineSegment(sketch, "E91.right", {"start": v(2.21, 25.48) * mm, "end": v(2.21, 28.22) * mm});
            skLineSegment(sketch, "E88.bottom", {"start": v(-2.98, 14.22) * mm, "end": v(-0.24, 14.22) * mm});
            skLineSegment(sketch, "E77.top", {"start": v(13.79, 35.91) * mm, "end": v(16.53, 35.91) * mm});
            skLineSegment(sketch, "E78.top", {"start": v(0.23, 11.5) * mm, "end": v(2.21, 11.5) * mm});
            skLineSegment(sketch, "E63.left", {"start": v(0.23, 5.2) * mm, "end": v(0.23, 7.95) * mm});
            skLineSegment(sketch, "E56.left", {"start": v(-2.98, 21.18) * mm, "end": v(-2.98, 19.2) * mm});
            skLineSegment(sketch, "E86.top", {"start": v(-6.53, 45.67) * mm, "end": v(-3.8, 45.67) * mm});
            skLineSegment(sketch, "E89.left", {"start": v(13.79, -2.5) * mm, "end": v(13.79, -4.47) * mm});
            skLineSegment(sketch, "E96.bottom", {"start": v(-6.53, -2.5) * mm, "end": v(-3.8, -2.5) * mm});
            skLineSegment(sketch, "E92.left", {"start": v(-6.53, 4.47) * mm, "end": v(-6.53, 2.49) * mm});
            skLineSegment(sketch, "E90.bottom", {"start": v(13.79, 14.22) * mm, "end": v(16.53, 14.22) * mm});
            skLineSegment(sketch, "E70.top", {"start": v(-16.54, 24.66) * mm, "end": v(-14.55, 24.66) * mm});
            skLineSegment(sketch, "E75.top", {"start": v(-6.53, 28.95) * mm, "end": v(-3.8, 28.95) * mm});
            skLineSegment(sketch, "E54.top", {"start": v(0.23, 24.66) * mm, "end": v(2.21, 24.66) * mm});
            skLineSegment(sketch, "E95.right", {"start": v(12.98, 21.18) * mm, "end": v(12.98, 19.2) * mm});
            skLineSegment(sketch, "E97.bottom", {"start": v(10.23, -2.5) * mm, "end": v(12.98, -2.5) * mm});
            skLineSegment(sketch, "E82.bottom", {"start": v(-2.98, -2.5) * mm, "end": v(-0.24, -2.5) * mm});
            skLineSegment(sketch, "E92.right", {"start": v(-3.8, 4.47) * mm, "end": v(-3.8, 2.49) * mm});
            skLineSegment(sketch, "E81.left", {"start": v(10.23, 4.47) * mm, "end": v(10.23, 2.49) * mm});
            skLineSegment(sketch, "E55.bottom", {"start": v(-16.54, 25.48) * mm, "end": v(-14.55, 25.48) * mm});
            skLineSegment(sketch, "E74.bottom", {"start": v(-2.98, 30.94) * mm, "end": v(-0.24, 30.94) * mm});
            skLineSegment(sketch, "E72.top", {"start": v(10.23, 45.67) * mm, "end": v(12.98, 45.67) * mm});
            skLineSegment(sketch, "E83.left", {"start": v(13.79, 47.65) * mm, "end": v(13.79, 45.67) * mm});
            skLineSegment(sketch, "E97.right", {"start": v(12.98, -2.5) * mm, "end": v(12.98, -4.47) * mm});
            skLineSegment(sketch, "E82.right", {"start": v(-0.24, -2.5) * mm, "end": v(-0.24, -4.47) * mm});
            skLineSegment(sketch, "E90.left", {"start": v(13.79, 14.22) * mm, "end": v(13.79, 12.24) * mm});
            skLineSegment(sketch, "E93.right", {"start": v(16.53, 21.18) * mm, "end": v(16.53, 19.2) * mm});
            skLineSegment(sketch, "E84.bottom", {"start": v(10.23, 30.94) * mm, "end": v(12.98, 30.94) * mm});
            skLineSegment(sketch, "E85.left", {"start": v(10.23, 37.9) * mm, "end": v(10.23, 35.91) * mm});
            skLineSegment(sketch, "E94.right", {"start": v(-3.8, 14.22) * mm, "end": v(-3.8, 12.24) * mm});
            skLineSegment(sketch, "E90.top", {"start": v(13.79, 12.24) * mm, "end": v(16.53, 12.24) * mm});
            skLineSegment(sketch, "E97.top", {"start": v(10.23, -4.47) * mm, "end": v(12.98, -4.47) * mm});
            skLineSegment(sketch, "E96.left", {"start": v(-6.53, -2.5) * mm, "end": v(-6.53, -4.47) * mm});
            skLineSegment(sketch, "E98.bottom", {"start": v(-6.53, 21.18) * mm, "end": v(-3.8, 21.18) * mm});
            skLineSegment(sketch, "E54.left", {"start": v(0.23, 21.92) * mm, "end": v(0.23, 24.66) * mm});
            skLineSegment(sketch, "E73.right", {"start": v(16.53, 30.94) * mm, "end": v(16.53, 28.95) * mm});
            skLineSegment(sketch, "E70.bottom", {"start": v(-16.54, 21.92) * mm, "end": v(-14.55, 21.92) * mm});
            skLineSegment(sketch, "E95.top", {"start": v(10.23, 19.2) * mm, "end": v(12.98, 19.2) * mm});
            skLineSegment(sketch, "E62.bottom", {"start": v(-2.98, 4.47) * mm, "end": v(-0.24, 4.47) * mm});
            skLineSegment(sketch, "E63.top", {"start": v(0.23, 7.95) * mm, "end": v(2.21, 7.95) * mm});
            skLineSegment(sketch, "E97.left", {"start": v(10.23, -2.5) * mm, "end": v(10.23, -4.47) * mm});
            skLineSegment(sketch, "E89.top", {"start": v(13.79, -4.47) * mm, "end": v(16.53, -4.47) * mm});
            skLineSegment(sketch, "E60.bottom", {"start": v(-2.98, 37.9) * mm, "end": v(-0.24, 37.9) * mm});
            skLineSegment(sketch, "E91.bottom", {"start": v(0.23, 25.48) * mm, "end": v(2.21, 25.48) * mm});
            skLineSegment(sketch, "E71.left", {"start": v(13.79, 4.47) * mm, "end": v(13.79, 2.49) * mm});
            skLineSegment(sketch, "E67.bottom", {"start": v(-2.98, -12.24) * mm, "end": v(-0.24, -12.24) * mm});
            skLineSegment(sketch, "E72.left", {"start": v(10.23, 47.65) * mm, "end": v(10.23, 45.67) * mm});
            skLineSegment(sketch, "E68.bottom", {"start": v(-16.54, -11.5) * mm, "end": v(-14.55, -11.5) * mm});
            skLineSegment(sketch, "E77.bottom", {"start": v(13.79, 37.9) * mm, "end": v(16.53, 37.9) * mm});
            skLineSegment(sketch, "E68.top", {"start": v(-16.54, -8.76) * mm, "end": v(-14.55, -8.76) * mm});
            skLineSegment(sketch, "E69.bottom", {"start": v(-6.53, -12.24) * mm, "end": v(-3.8, -12.24) * mm});
            skLineSegment(sketch, "E99.bottom", {"start": v(-16.54, -7.95) * mm, "end": v(-14.55, -7.95) * mm});
            skLineSegment(sketch, "E99.top", {"start": v(-16.54, -5.2) * mm, "end": v(-14.55, -5.2) * mm});
            skLineSegment(sketch, "E99.left", {"start": v(-16.54, -7.95) * mm, "end": v(-16.54, -5.2) * mm});
            skLineSegment(sketch, "E99.right", {"start": v(-14.55, -7.95) * mm, "end": v(-14.55, -5.2) * mm});
            skLineSegment(sketch, "E94.left", {"start": v(-6.53, 14.22) * mm, "end": v(-6.53, 12.24) * mm});
            skLineSegment(sketch, "E71.right", {"start": v(16.53, 4.47) * mm, "end": v(16.53, 2.49) * mm});
            skLineSegment(sketch, "E87.right", {"start": v(-14.55, 42.19) * mm, "end": v(-14.55, 44.93) * mm});
            skLineSegment(sketch, "E84.left", {"start": v(10.23, 30.94) * mm, "end": v(10.23, 28.95) * mm});
            skLineSegment(sketch, "E70.left", {"start": v(-16.54, 21.92) * mm, "end": v(-16.54, 24.66) * mm});
            skLineSegment(sketch, "E62.left", {"start": v(-2.98, 4.47) * mm, "end": v(-2.98, 2.49) * mm});
            skLineSegment(sketch, "E85.right", {"start": v(12.98, 37.9) * mm, "end": v(12.98, 35.91) * mm});
            skLineSegment(sketch, "E65.bottom", {"start": v(-16.54, 38.63) * mm, "end": v(-14.55, 38.63) * mm});
            skLineSegment(sketch, "E95.bottom", {"start": v(10.23, 21.18) * mm, "end": v(12.98, 21.18) * mm});
            skLineSegment(sketch, "E94.bottom", {"start": v(-6.53, 14.22) * mm, "end": v(-3.8, 14.22) * mm});
            skLineSegment(sketch, "E59.left", {"start": v(-16.54, 5.2) * mm, "end": v(-16.54, 7.95) * mm});
            skLineSegment(sketch, "E76.right", {"start": v(2.21, -7.95) * mm, "end": v(2.21, -5.2) * mm});
            skLineSegment(sketch, "E89.right", {"start": v(16.53, -2.5) * mm, "end": v(16.53, -4.47) * mm});
            skLineSegment(sketch, "E93.bottom", {"start": v(13.79, 21.18) * mm, "end": v(16.53, 21.18) * mm});
            skLineSegment(sketch, "E79.right", {"start": v(12.98, 14.22) * mm, "end": v(12.98, 12.24) * mm});
            skLineSegment(sketch, "E87.bottom", {"start": v(-16.54, 42.19) * mm, "end": v(-14.55, 42.19) * mm});
            skLineSegment(sketch, "E98.right", {"start": v(-3.8, 21.18) * mm, "end": v(-3.8, 19.2) * mm});
            skLineSegment(sketch, "E83.bottom", {"start": v(13.79, 47.65) * mm, "end": v(16.53, 47.65) * mm});
            skLineSegment(sketch, "E80.left", {"start": v(-2.98, 47.65) * mm, "end": v(-2.98, 45.67) * mm});
            skLineSegment(sketch, "E100.bottom", {"start": v(-6.53, 37.9) * mm, "end": v(-3.8, 37.9) * mm});
            skLineSegment(sketch, "E88.left", {"start": v(-2.98, 14.22) * mm, "end": v(-2.98, 12.24) * mm});
            skLineSegment(sketch, "E100.left", {"start": v(-6.53, 37.9) * mm, "end": v(-6.53, 35.91) * mm});
            skLineSegment(sketch, "E96.right", {"start": v(-3.8, -2.5) * mm, "end": v(-3.8, -4.47) * mm});
            skLineSegment(sketch, "E80.right", {"start": v(-0.24, 47.65) * mm, "end": v(-0.24, 45.67) * mm});
            skLineSegment(sketch, "E92.top", {"start": v(-6.53, 2.49) * mm, "end": v(-3.8, 2.49) * mm});
            skLineSegment(sketch, "E98.left", {"start": v(-6.53, 21.18) * mm, "end": v(-6.53, 19.2) * mm});
            skLineSegment(sketch, "E86.right", {"start": v(-3.8, 47.65) * mm, "end": v(-3.8, 45.67) * mm});
            skLineSegment(sketch, "E88.top", {"start": v(-2.98, 12.24) * mm, "end": v(-0.24, 12.24) * mm});
            skLineSegment(sketch, "E100.top", {"start": v(-6.53, 35.91) * mm, "end": v(-3.8, 35.91) * mm});
            skLineSegment(sketch, "E80.top", {"start": v(-2.98, 45.67) * mm, "end": v(-0.24, 45.67) * mm});
            skLineSegment(sketch, "E100.right", {"start": v(-3.8, 37.9) * mm, "end": v(-3.8, 35.91) * mm});
            skLineSegment(sketch, "E60.left", {"start": v(-2.98, 37.9) * mm, "end": v(-2.98, 35.91) * mm});
            skLineSegment(sketch, "E98.top", {"start": v(-6.53, 19.2) * mm, "end": v(-3.8, 19.2) * mm});
            skLineSegment(sketch, "E101.top", {"start": v(-2.98, 69.34) * mm, "end": v(-0.24, 69.34) * mm});
            skLineSegment(sketch, "E102.top", {"start": v(0.23, 61.64) * mm, "end": v(2.21, 61.64) * mm});
            skLineSegment(sketch, "E103.top", {"start": v(0.23, 58.09) * mm, "end": v(2.21, 58.09) * mm});
            skLineSegment(sketch, "E104.top", {"start": v(0.23, 74.8) * mm, "end": v(2.21, 74.8) * mm});
            skLineSegment(sketch, "E105.top", {"start": v(-16.54, 58.09) * mm, "end": v(-14.55, 58.09) * mm});
            skLineSegment(sketch, "E102.bottom", {"start": v(0.23, 58.9) * mm, "end": v(2.21, 58.9) * mm});
            skLineSegment(sketch, "E105.left", {"start": v(-16.54, 55.35) * mm, "end": v(-16.54, 58.09) * mm});
            skLineSegment(sketch, "E106.top", {"start": v(-16.54, 78.36) * mm, "end": v(-14.55, 78.36) * mm});
            skLineSegment(sketch, "E107.top", {"start": v(13.79, 52.63) * mm, "end": v(16.53, 52.63) * mm});
            skLineSegment(sketch, "E106.bottom", {"start": v(-16.54, 75.61) * mm, "end": v(-14.55, 75.61) * mm});
            skLineSegment(sketch, "E108.top", {"start": v(-2.98, 52.63) * mm, "end": v(-0.24, 52.63) * mm});
            skLineSegment(sketch, "E109.top", {"start": v(-16.54, 74.8) * mm, "end": v(-14.55, 74.8) * mm});
            skLineSegment(sketch, "E110.top", {"start": v(-16.54, 61.64) * mm, "end": v(-14.55, 61.64) * mm});
            skLineSegment(sketch, "E104.right", {"start": v(2.21, 72.06) * mm, "end": v(2.21, 74.8) * mm});
            skLineSegment(sketch, "E111.right", {"start": v(16.53, 71.32) * mm, "end": v(16.53, 69.34) * mm});
            skLineSegment(sketch, "E103.bottom", {"start": v(0.23, 55.35) * mm, "end": v(2.21, 55.35) * mm});
            skLineSegment(sketch, "E112.right", {"start": v(16.53, 81.07) * mm, "end": v(16.53, 79.1) * mm});
            skLineSegment(sketch, "E113.top", {"start": v(13.79, 62.38) * mm, "end": v(16.53, 62.38) * mm});
            skLineSegment(sketch, "E109.right", {"start": v(-14.55, 72.06) * mm, "end": v(-14.55, 74.8) * mm});
            skLineSegment(sketch, "E104.left", {"start": v(0.23, 72.06) * mm, "end": v(0.23, 74.8) * mm});
            skLineSegment(sketch, "E112.top", {"start": v(13.79, 79.1) * mm, "end": v(16.53, 79.1) * mm});
            skLineSegment(sketch, "E114.bottom", {"start": v(0.23, 75.61) * mm, "end": v(2.21, 75.61) * mm});
            skLineSegment(sketch, "E115.top", {"start": v(-2.98, 62.38) * mm, "end": v(-0.24, 62.38) * mm});
            skLineSegment(sketch, "E109.bottom", {"start": v(-16.54, 72.06) * mm, "end": v(-14.55, 72.06) * mm});
            skLineSegment(sketch, "E101.right", {"start": v(-0.24, 71.32) * mm, "end": v(-0.24, 69.34) * mm});
            skLineSegment(sketch, "E104.bottom", {"start": v(0.23, 72.06) * mm, "end": v(2.21, 72.06) * mm});
            skLineSegment(sketch, "E105.right", {"start": v(-14.55, 55.35) * mm, "end": v(-14.55, 58.09) * mm});
            skLineSegment(sketch, "E103.right", {"start": v(2.21, 55.35) * mm, "end": v(2.21, 58.09) * mm});
            skLineSegment(sketch, "E109.left", {"start": v(-16.54, 72.06) * mm, "end": v(-16.54, 74.8) * mm});
            skLineSegment(sketch, "E103.left", {"start": v(0.23, 55.35) * mm, "end": v(0.23, 58.09) * mm});
            skLineSegment(sketch, "E111.top", {"start": v(13.79, 69.34) * mm, "end": v(16.53, 69.34) * mm});
            skLineSegment(sketch, "E110.bottom", {"start": v(-16.54, 58.9) * mm, "end": v(-14.55, 58.9) * mm});
            skLineSegment(sketch, "E114.top", {"start": v(0.23, 78.36) * mm, "end": v(2.21, 78.36) * mm});
            skLineSegment(sketch, "E105.bottom", {"start": v(-16.54, 55.35) * mm, "end": v(-14.55, 55.35) * mm});
            skLineSegment(sketch, "E116.top", {"start": v(-2.98, 79.1) * mm, "end": v(-0.24, 79.1) * mm});
            skLineSegment(sketch, "E112.left", {"start": v(13.79, 81.07) * mm, "end": v(13.79, 79.1) * mm});
            skLineSegment(sketch, "E117.top", {"start": v(-6.53, 79.1) * mm, "end": v(-3.8, 79.1) * mm});
            skLineSegment(sketch, "E118.bottom", {"start": v(-6.53, 64.36) * mm, "end": v(-3.8, 64.36) * mm});
            skLineSegment(sketch, "E119.left", {"start": v(10.23, 71.32) * mm, "end": v(10.23, 69.34) * mm});
            skLineSegment(sketch, "E114.right", {"start": v(2.21, 75.61) * mm, "end": v(2.21, 78.36) * mm});
            skLineSegment(sketch, "E118.top", {"start": v(-6.53, 62.38) * mm, "end": v(-3.8, 62.38) * mm});
            skLineSegment(sketch, "E101.left", {"start": v(-2.98, 71.32) * mm, "end": v(-2.98, 69.34) * mm});
            skLineSegment(sketch, "E120.left", {"start": v(-6.53, 71.32) * mm, "end": v(-6.53, 69.34) * mm});
            skLineSegment(sketch, "E119.right", {"start": v(12.98, 71.32) * mm, "end": v(12.98, 69.34) * mm});
            skLineSegment(sketch, "E106.left", {"start": v(-16.54, 75.61) * mm, "end": v(-16.54, 78.36) * mm});
            skLineSegment(sketch, "E121.bottom", {"start": v(10.23, 64.36) * mm, "end": v(12.98, 64.36) * mm});
            skLineSegment(sketch, "E117.left", {"start": v(-6.53, 81.07) * mm, "end": v(-6.53, 79.1) * mm});
            skLineSegment(sketch, "E120.bottom", {"start": v(-6.53, 71.32) * mm, "end": v(-3.8, 71.32) * mm});
            skLineSegment(sketch, "E101.bottom", {"start": v(-2.98, 71.32) * mm, "end": v(-0.24, 71.32) * mm});
            skLineSegment(sketch, "E119.top", {"start": v(10.23, 69.34) * mm, "end": v(12.98, 69.34) * mm});
            skLineSegment(sketch, "E110.right", {"start": v(-14.55, 58.9) * mm, "end": v(-14.55, 61.64) * mm});
            skLineSegment(sketch, "E116.left", {"start": v(-2.98, 81.07) * mm, "end": v(-2.98, 79.1) * mm});
            skLineSegment(sketch, "E106.right", {"start": v(-14.55, 75.61) * mm, "end": v(-14.55, 78.36) * mm});
            skLineSegment(sketch, "E121.top", {"start": v(10.23, 62.38) * mm, "end": v(12.98, 62.38) * mm});
            skLineSegment(sketch, "E112.bottom", {"start": v(13.79, 81.07) * mm, "end": v(16.53, 81.07) * mm});
            skLineSegment(sketch, "E111.left", {"start": v(13.79, 71.32) * mm, "end": v(13.79, 69.34) * mm});
            skLineSegment(sketch, "E119.bottom", {"start": v(10.23, 71.32) * mm, "end": v(12.98, 71.32) * mm});
            skLineSegment(sketch, "E122.top", {"start": v(-6.53, 52.63) * mm, "end": v(-3.8, 52.63) * mm});
            skLineSegment(sketch, "E114.left", {"start": v(0.23, 75.61) * mm, "end": v(0.23, 78.36) * mm});
            skLineSegment(sketch, "E120.right", {"start": v(-3.8, 71.32) * mm, "end": v(-3.8, 69.34) * mm});
            skLineSegment(sketch, "E123.top", {"start": v(10.23, 79.1) * mm, "end": v(12.98, 79.1) * mm});
            skLineSegment(sketch, "E124.top", {"start": v(10.23, 52.63) * mm, "end": v(12.98, 52.63) * mm});
            skLineSegment(sketch, "E123.left", {"start": v(10.23, 81.07) * mm, "end": v(10.23, 79.1) * mm});
            skLineSegment(sketch, "E116.right", {"start": v(-0.24, 81.07) * mm, "end": v(-0.24, 79.1) * mm});
            skLineSegment(sketch, "E108.bottom", {"start": v(-2.98, 54.6) * mm, "end": v(-0.24, 54.6) * mm});
            skLineSegment(sketch, "E116.bottom", {"start": v(-2.98, 81.07) * mm, "end": v(-0.24, 81.07) * mm});
            skLineSegment(sketch, "E102.left", {"start": v(0.23, 58.9) * mm, "end": v(0.23, 61.64) * mm});
            skLineSegment(sketch, "E124.bottom", {"start": v(10.23, 54.6) * mm, "end": v(12.98, 54.6) * mm});
            skLineSegment(sketch, "E102.right", {"start": v(2.21, 58.9) * mm, "end": v(2.21, 61.64) * mm});
            skLineSegment(sketch, "E111.bottom", {"start": v(13.79, 71.32) * mm, "end": v(16.53, 71.32) * mm});
            skLineSegment(sketch, "E110.left", {"start": v(-16.54, 58.9) * mm, "end": v(-16.54, 61.64) * mm});
            skLineSegment(sketch, "E122.bottom", {"start": v(-6.53, 54.6) * mm, "end": v(-3.8, 54.6) * mm});
            skLineSegment(sketch, "E117.right", {"start": v(-3.8, 81.07) * mm, "end": v(-3.8, 79.1) * mm});
            skLineSegment(sketch, "E123.bottom", {"start": v(10.23, 81.07) * mm, "end": v(12.98, 81.07) * mm});
            skLineSegment(sketch, "E117.bottom", {"start": v(-6.53, 81.07) * mm, "end": v(-3.8, 81.07) * mm});
            skLineSegment(sketch, "E113.bottom", {"start": v(13.79, 64.36) * mm, "end": v(16.53, 64.36) * mm});
            skLineSegment(sketch, "E120.top", {"start": v(-6.53, 69.34) * mm, "end": v(-3.8, 69.34) * mm});
            skLineSegment(sketch, "E123.right", {"start": v(12.98, 81.07) * mm, "end": v(12.98, 79.1) * mm});
            skLineSegment(sketch, "E115.bottom", {"start": v(-2.98, 64.36) * mm, "end": v(-0.24, 64.36) * mm});
            skLineSegment(sketch, "E107.bottom", {"start": v(13.79, 54.6) * mm, "end": v(16.53, 54.6) * mm});
            skLineSegment(sketch, "E108.right", {"start": v(-0.24, 54.6) * mm, "end": v(-0.24, 52.63) * mm});
            skLineSegment(sketch, "E107.right", {"start": v(16.53, 54.6) * mm, "end": v(16.53, 52.63) * mm});
            skLineSegment(sketch, "E121.left", {"start": v(10.23, 64.36) * mm, "end": v(10.23, 62.38) * mm});
            skLineSegment(sketch, "E115.left", {"start": v(-2.98, 64.36) * mm, "end": v(-2.98, 62.38) * mm});
            skLineSegment(sketch, "E115.right", {"start": v(-0.24, 64.36) * mm, "end": v(-0.24, 62.38) * mm});
            skLineSegment(sketch, "E124.left", {"start": v(10.23, 54.6) * mm, "end": v(10.23, 52.63) * mm});
            skLineSegment(sketch, "E122.right", {"start": v(-3.8, 54.6) * mm, "end": v(-3.8, 52.63) * mm});
            skLineSegment(sketch, "E108.left", {"start": v(-2.98, 54.6) * mm, "end": v(-2.98, 52.63) * mm});
            skLineSegment(sketch, "E124.right", {"start": v(12.98, 54.6) * mm, "end": v(12.98, 52.63) * mm});
            skLineSegment(sketch, "E118.left", {"start": v(-6.53, 64.36) * mm, "end": v(-6.53, 62.38) * mm});
            skLineSegment(sketch, "E113.left", {"start": v(13.79, 64.36) * mm, "end": v(13.79, 62.38) * mm});
            skLineSegment(sketch, "E107.left", {"start": v(13.79, 54.6) * mm, "end": v(13.79, 52.63) * mm});
            skLineSegment(sketch, "E122.left", {"start": v(-6.53, 54.6) * mm, "end": v(-6.53, 52.63) * mm});
            skLineSegment(sketch, "E121.right", {"start": v(12.98, 64.36) * mm, "end": v(12.98, 62.38) * mm});
            skLineSegment(sketch, "E118.right", {"start": v(-3.8, 64.36) * mm, "end": v(-3.8, 62.38) * mm});
            skLineSegment(sketch, "E113.right", {"start": v(16.53, 64.36) * mm, "end": v(16.53, 62.38) * mm});
            skSolve(sketch);
        }
        {
            var Q0;
            Q0=qSketchRegion(id+"F2",true);
            extrude(context, id + "F3", {"entities" : qUnion([Q0]), "operationType" : NewBodyOperationType.REMOVE, "oppositeDirection" : true, "depth" : 3 * mm});
        }
    });
